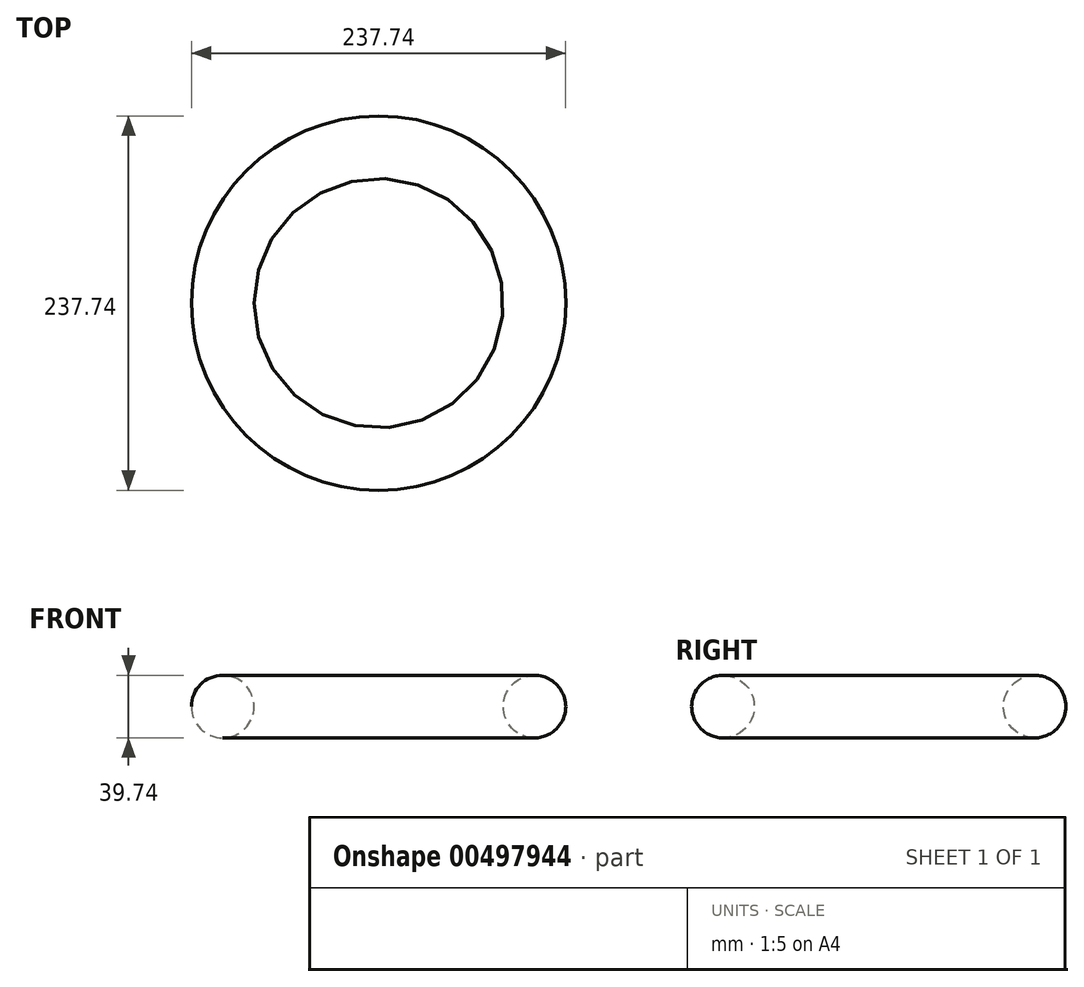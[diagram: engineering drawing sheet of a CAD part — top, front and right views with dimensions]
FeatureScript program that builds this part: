
annotation { "Feature Type Name" : "Feature", "Feature Type Description" : "" }
export const myFeature = defineFeature(function(context is Context, id is Id, definition is map)
    precondition{}
    {
        {
            var Q0;
            Q0=qCreatedBy(makeId("Front.planeOp"),FACE);
            var sketch = newSketch(context, id + "F0", { "sketchPlane" : qUnion([Q0])});
            skLineSegment(sketch, "E0", {"start": v(0, 0) * mm, "end": v(0, 44.03) * mm, "construction": true});
            skCircle(sketch, "E1", {"center": v(99, 27.63) * mm, "radius": 19.87 * mm});
            skSolve(sketch);
        }
        {
            var Q0;
            Q0=makeQuery(id+"F0.imprint","IMPRINT",FACE,{"disambiguationData":[TD([[makeQuery(id+"F0.imprint","IMPRINT",EDGE,{"derivedFrom":sQuery(id+"F0.wireOp",EDGE,"E1")}),1.0]])]});
            var Q1;
            Q1=sQuery(id+"F0.wireOp",EDGE,"E0");
            revolve(context, id + "F1", {"entities" : qUnion([Q0]), "axis" : qUnion([Q1]), "revolveType" : RevolveType.FULL});
        }
    });
